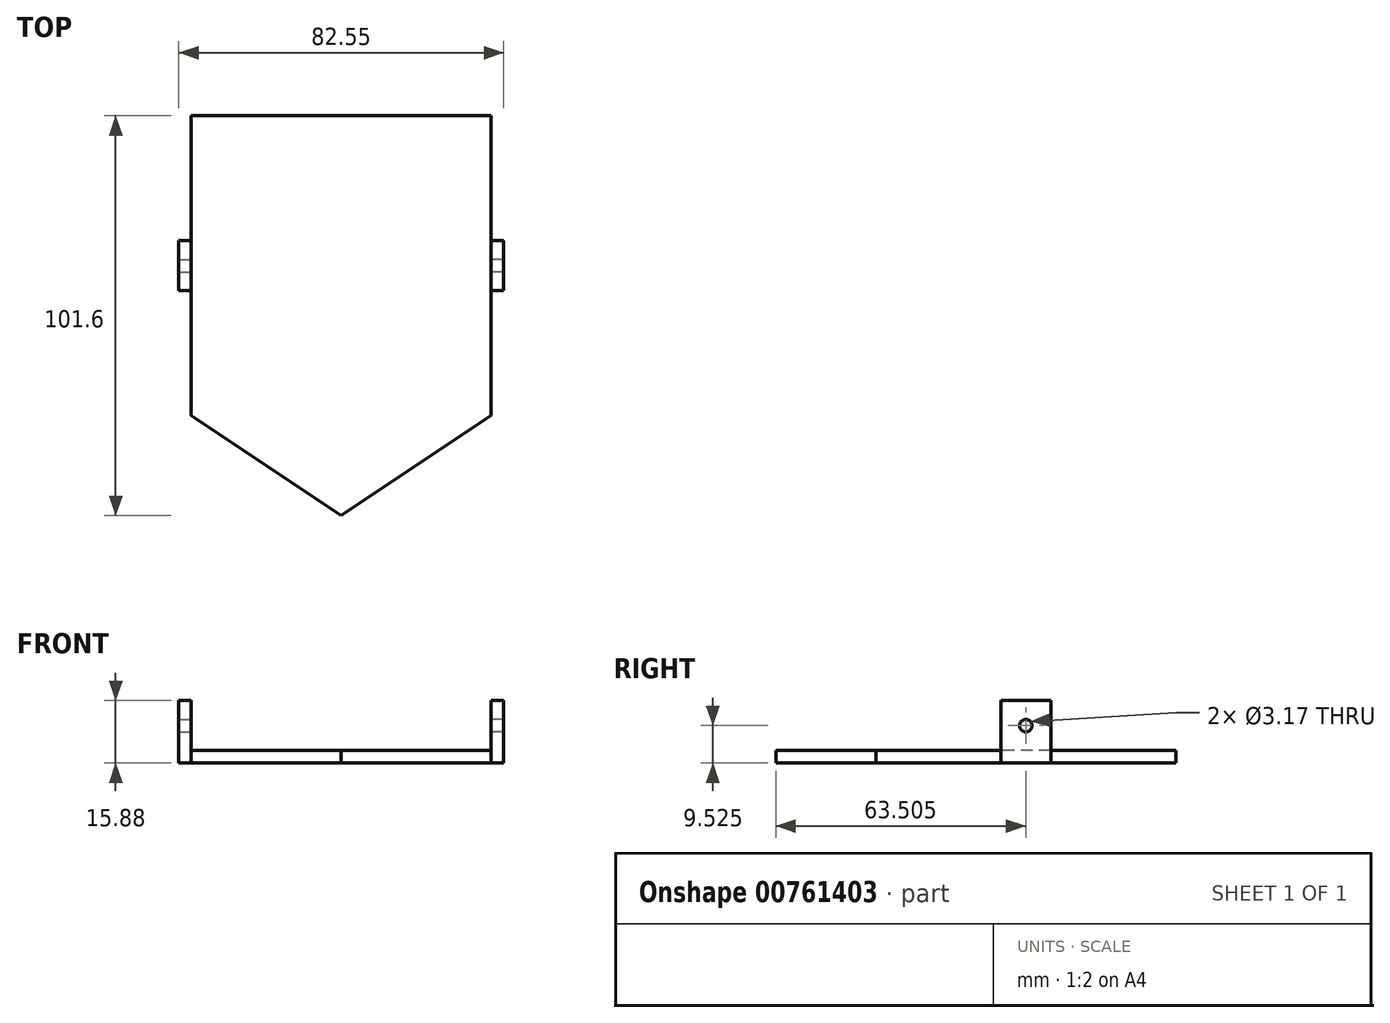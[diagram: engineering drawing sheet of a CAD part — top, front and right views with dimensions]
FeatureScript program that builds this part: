
annotation { "Feature Type Name" : "Feature", "Feature Type Description" : "" }
export const myFeature = defineFeature(function(context is Context, id is Id, definition is map)
    precondition{}
    {
        {
            var Q0;
            Q0=qCreatedBy(makeId("Top.planeOp"),FACE);
            var sketch = newSketch(context, id + "F0", { "sketchPlane" : qUnion([Q0])});
            skLineSegment(sketch, "E0.bottom", {"start": v(-46.37, 66.57) * mm, "end": v(29.83, 66.57) * mm});
            skLineSegment(sketch, "E0.left", {"start": v(-46.37, 66.57) * mm, "end": v(-46.37, -9.63) * mm});
            skLineSegment(sketch, "E0.right", {"start": v(29.83, 66.57) * mm, "end": v(29.83, -9.63) * mm});
            skLineSegment(sketch, "E1", {"start": v(-46.37, -9.63) * mm, "end": v(-8.27, -35.03) * mm});
            skLineSegment(sketch, "E2", {"start": v(-8.27, -35.03) * mm, "end": v(29.83, -9.63) * mm});
            skPoint(sketch, "E3.orphan", {"position": v(-46.37, -35.03) * mm});
            skPoint(sketch, "E0.top.end.orphan", {"position": v(29.83, -35.03) * mm});
            skSolve(sketch);
        }
        {
            var Q0;
            Q0=makeQuery(id+"F0.imprint","IMPRINT",FACE,{"disambiguationData":[TD([[makeQuery(id+"F0.imprint","IMPRINT",EDGE,{"derivedFrom":sQuery(id+"F0.wireOp",EDGE,"E0.bottom")}),-1.0]])]});
            extrude(context, id + "F1", {"entities" : qUnion([Q0]), "depth" : 3.17 * mm, "offsetDistance" : 25.4 * mm});
        }
        {
            var Q0;
            Q0=makeQuery(id+"F1.opExtrude","SWEPT_FACE",FACE,{"disambiguationData":[OSD([sQuery(id+"F0.wireOp",EDGE,"E0.left")])]});
            var sketch = newSketch(context, id + "F2", { "sketchPlane" : qUnion([Q0])});
            skLineSegment(sketch, "E4.bottom", {"start": v(-22.12, 3.18) * mm, "end": v(-34.82, 3.18) * mm});
            skLineSegment(sketch, "E4.top", {"start": v(-22.12, 15.88) * mm, "end": v(-34.82, 15.88) * mm});
            skLineSegment(sketch, "E4.left", {"start": v(-22.12, 3.18) * mm, "end": v(-22.12, 15.88) * mm});
            skLineSegment(sketch, "E4.right", {"start": v(-34.82, 3.17) * mm, "end": v(-34.82, 15.87) * mm});
            skPoint(sketch, "E4.middle", {"position": v(-28.47, 9.52) * mm});
            skCircle(sketch, "E5", {"center": v(-28.47, 9.52) * mm, "radius": 1.59 * mm});
            skSolve(sketch);
        }
        {
            var Q0;
            Q0=makeQuery(id+"F1.opExtrude","SWEPT_FACE",FACE,{"disambiguationData":[OSD([sQuery(id+"F0.wireOp",EDGE,"E0.right")])]});
            var sketch = newSketch(context, id + "F3", { "sketchPlane" : qUnion([Q0])});
            skLineSegment(sketch, "E6.bottom", {"start": v(22.12, 15.87) * mm, "end": v(34.82, 15.87) * mm});
            skLineSegment(sketch, "E6.top", {"start": v(22.12, 3.17) * mm, "end": v(34.82, 3.17) * mm});
            skLineSegment(sketch, "E6.left", {"start": v(22.12, 15.87) * mm, "end": v(22.12, 3.17) * mm});
            skLineSegment(sketch, "E6.right", {"start": v(34.82, 15.88) * mm, "end": v(34.82, 3.18) * mm});
            skPoint(sketch, "E6.middle", {"position": v(28.47, 9.53) * mm});
            skCircle(sketch, "E7", {"center": v(28.47, 9.53) * mm, "radius": 1.59 * mm});
            skSolve(sketch);
        }
        {
            var Q0;
            Q0 = qSketchRegion(id + "F2", true);
            extrude(context, id + "F4", {"entities" : qUnion([Q0]), "depth" : 3.17 * mm, "offsetDistance" : 25.4 * mm});
        }
        {
            var Q0;
            Q0=makeQuery(id+"F4.opExtrude","SWEPT_FACE",FACE,{"disambiguationData":[OSD([sQuery(id+"F2.wireOp",EDGE,"E4.bottom")])]});
            extrude(context, id + "F5", {"entities" : qUnion([Q0]), "operationType" : NewBodyOperationType.ADD, "depth" : 3.17 * mm, "offsetDistance" : 25.4 * mm});
        }
        {
            var Q0;
            Q0=makeQuery(id+"F3.imprint","IMPRINT",FACE,{"disambiguationData":[TD([[makeQuery(id+"F3.imprint","IMPRINT",EDGE,{"derivedFrom":sQuery(id+"F3.wireOp",EDGE,"E6.bottom")}),-1.0]])]});
            extrude(context, id + "F6", {"entities" : qUnion([Q0]), "depth" : 3.17 * mm, "offsetDistance" : 25.4 * mm});
        }
        {
            var Q0;
            Q0=makeQuery(id+"F6.opExtrude","SWEPT_FACE",FACE,{"disambiguationData":[OSD([sQuery(id+"F3.wireOp",EDGE,"E6.top")])]});
            extrude(context, id + "F7", {"entities" : qUnion([Q0]), "operationType" : NewBodyOperationType.ADD, "depth" : 3.17 * mm, "offsetDistance" : 25.4 * mm});
        }
    });
